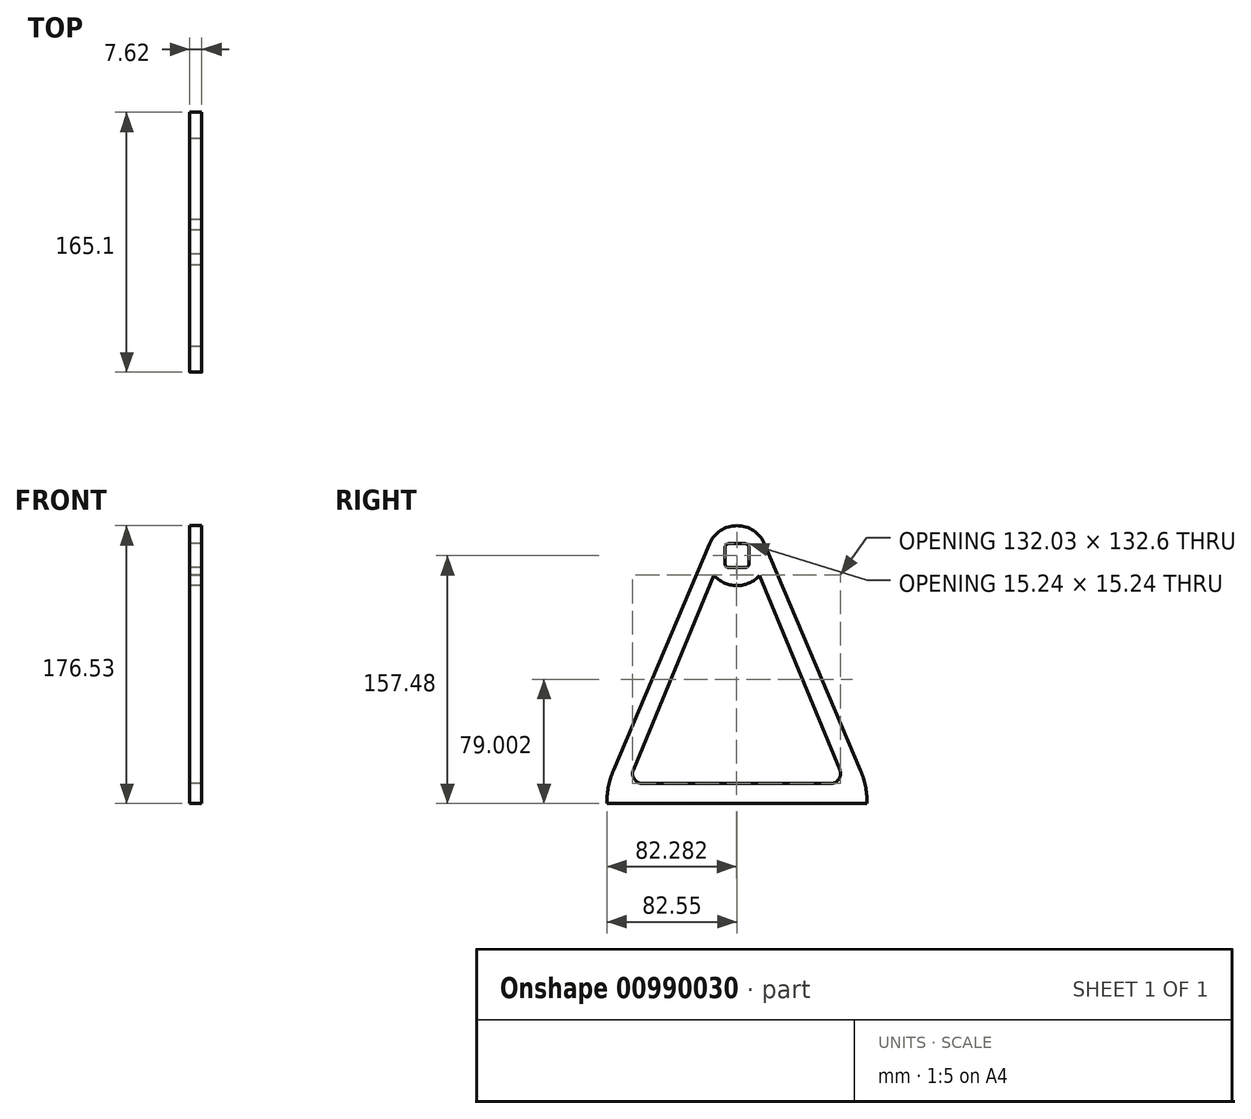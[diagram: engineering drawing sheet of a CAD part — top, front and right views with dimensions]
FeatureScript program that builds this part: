
annotation { "Feature Type Name" : "Feature", "Feature Type Description" : "" }
export const myFeature = defineFeature(function(context is Context, id is Id, definition is map)
    precondition{}
    {
        {
            var Q0;
            Q0=qCreatedBy(makeId("Right.planeOp"),FACE);
            var sketch = newSketch(context, id + "F0", { "sketchPlane" : qUnion([Q0])});
            skLineSegment(sketch, "E0.bottom", {"start": v(-3.81, 6.35) * mm, "end": v(3.81, 6.35) * mm});
            skLineSegment(sketch, "E0.top", {"start": v(-3.81, -6.35) * mm, "end": v(3.81, -6.35) * mm});
            skLineSegment(sketch, "E0.left", {"start": v(-6.35, 3.81) * mm, "end": v(-6.35, -3.81) * mm});
            skLineSegment(sketch, "E0.right", {"start": v(6.35, 3.81) * mm, "end": v(6.35, -3.81) * mm});
            skLineSegment(sketch, "E1.bottom", {"start": v(-4.76, 4.76) * mm, "end": v(4.76, 4.76) * mm});
            skLineSegment(sketch, "E1.top", {"start": v(-4.76, -4.76) * mm, "end": v(4.76, -4.76) * mm});
            skLineSegment(sketch, "E1.left", {"start": v(-4.76, 4.76) * mm, "end": v(-4.76, -4.76) * mm});
            skLineSegment(sketch, "E1.right", {"start": v(4.76, 4.76) * mm, "end": v(4.76, -4.76) * mm});
            skPoint(sketch, "E2.visualSharp", {"position": v(-6.35, 6.35) * mm});
            skArc(sketch, "E2.filletArc", {"start": v(-3.81, 6.35) * mm, "mid": v(-5.6, 5.6) * mm, "end": v(-6.35, 3.81) * mm});
            skPoint(sketch, "E3.visualSharp", {"position": v(6.35, 6.35) * mm});
            skArc(sketch, "E3.filletArc", {"start": v(6.35, 3.81) * mm, "mid": v(5.6, 5.6) * mm, "end": v(3.81, 6.35) * mm});
            skPoint(sketch, "E4.visualSharp", {"position": v(6.35, -6.35) * mm});
            skArc(sketch, "E4.filletArc", {"start": v(3.81, -6.35) * mm, "mid": v(5.6, -5.6) * mm, "end": v(6.35, -3.81) * mm});
            skPoint(sketch, "E5.visualSharp", {"position": v(-6.35, -6.35) * mm});
            skArc(sketch, "E5.filletArc", {"start": v(-6.35, -3.81) * mm, "mid": v(-5.6, -5.6) * mm, "end": v(-3.81, -6.35) * mm});
            skSolve(sketch);
        }
        {
            var Q0;
            Q0=qCreatedBy(makeId("Right.planeOp"),FACE);
            var sketch = newSketch(context, id + "F1", { "sketchPlane" : qUnion([Q0])});
            skLineSegment(sketch, "E6.bottom", {"start": v(0, -144.78) * mm, "end": v(59.43, -144.78) * mm});
            skLineSegment(sketch, "E6.top", {"start": v(0, -157.48) * mm, "end": v(82.55, -157.48) * mm});
            skLineSegment(sketch, "E6.right", {"start": v(82.55, -156.36) * mm, "end": v(82.55, -157.48) * mm});
            skLineSegment(sketch, "E7.MirrorCS", {"start": v(0, -144.78) * mm, "end": v(-59.96, -144.78) * mm});
            skLineSegment(sketch, "E8.MirrorCS", {"start": v(-82.55, -156.36) * mm, "end": v(-82.55, -157.48) * mm});
            skLineSegment(sketch, "E9.MirrorCS", {"start": v(0, -157.48) * mm, "end": v(-82.55, -157.48) * mm});
            skLineSegment(sketch, "E10", {"start": v(17.55, 7.42) * mm, "end": v(78.53, -136.55) * mm});
            skLineSegment(sketch, "E11", {"start": v(-17.54, 7.43) * mm, "end": v(-78.53, -136.55) * mm});
            skCircle(sketch, "E12", {"center": v(0, 0) * mm, "radius": 19.05 * mm});
            skLineSegment(sketch, "E13", {"start": v(14.29, -12.6) * mm, "end": v(65.3, -136) * mm});
            skLineSegment(sketch, "E14", {"start": v(-14.65, -12.18) * mm, "end": v(-65.83, -136) * mm});
            skPoint(sketch, "E15.visualSharp", {"position": v(-82.55, -146.05) * mm});
            skArc(sketch, "E15.filletArc", {"start": v(-78.53, -136.55) * mm, "mid": v(-81.53, -146.26) * mm, "end": v(-82.55, -156.36) * mm});
            skPoint(sketch, "E16.visualSharp", {"position": v(82.55, -146.05) * mm});
            skArc(sketch, "E16.filletArc", {"start": v(82.55, -156.36) * mm, "mid": v(81.53, -146.26) * mm, "end": v(78.53, -136.55) * mm});
            skPoint(sketch, "E17.newPointB", {"position": v(82.55, -144.78) * mm});
            skArc(sketch, "E17.filletArc", {"start": v(59.43, -144.78) * mm, "mid": v(64.7, -141.96) * mm, "end": v(65.3, -136) * mm});
            skPoint(sketch, "E18.newPointB", {"position": v(-82.55, -144.78) * mm});
            skArc(sketch, "E18.filletArc", {"start": v(-65.83, -136) * mm, "mid": v(-65.24, -141.96) * mm, "end": v(-59.96, -144.78) * mm});
            skLineSegment(sketch, "E19.bottom", {"start": v(-5.08, 7.62) * mm, "end": v(5.08, 7.62) * mm});
            skLineSegment(sketch, "E19.top", {"start": v(-5.08, -7.62) * mm, "end": v(5.08, -7.62) * mm});
            skLineSegment(sketch, "E19.left", {"start": v(-7.62, 5.08) * mm, "end": v(-7.62, -5.08) * mm});
            skLineSegment(sketch, "E19.right", {"start": v(7.62, 5.08) * mm, "end": v(7.62, -5.08) * mm});
            skPoint(sketch, "E20.visualSharp", {"position": v(-7.62, -7.62) * mm});
            skArc(sketch, "E20.filletArc", {"start": v(-7.62, -5.08) * mm, "mid": v(-6.88, -6.88) * mm, "end": v(-5.08, -7.62) * mm});
            skPoint(sketch, "E21.visualSharp", {"position": v(7.62, 7.62) * mm});
            skArc(sketch, "E21.filletArc", {"start": v(7.62, 5.08) * mm, "mid": v(6.88, 6.88) * mm, "end": v(5.08, 7.62) * mm});
            skPoint(sketch, "E22.visualSharp", {"position": v(-7.62, 7.62) * mm});
            skArc(sketch, "E22.filletArc", {"start": v(-5.08, 7.62) * mm, "mid": v(-6.88, 6.88) * mm, "end": v(-7.62, 5.08) * mm});
            skPoint(sketch, "E23.visualSharp", {"position": v(7.62, -7.62) * mm});
            skArc(sketch, "E23.filletArc", {"start": v(5.08, -7.62) * mm, "mid": v(6.88, -6.88) * mm, "end": v(7.62, -5.08) * mm});
            skSolve(sketch);
        }
        {
            var Q0;
            Q0=makeQuery(id+"F1.imprint","IMPRINT",FACE,{"disambiguationData":[TD([[makeQuery(id+"F1.imprint","IMPRINT",EDGE,{"derivedFrom":sQuery(id+"F1.wireOp",EDGE,"19484ca9-c6df-4c4f-9a82-6452225bbd83")}),-1.0]])]});
            var Q1;
            Q1=makeQuery(id+"F1.imprint","IMPRINT",FACE,{"disambiguationData":[TD([[makeQuery(id+"F1.imprint","IMPRINT",EDGE,{"derivedFrom":sQuery(id+"F1.wireOp",EDGE,"E6.bottom")}),-1.0]])]});
            extrude(context, id + "F2", {"entities" : qUnion([Q0, Q1]), "depth" : 7.62 * mm, "offsetDistance" : 25.4 * mm});
        }
        {
            var Q0;
            Q0=makeQuery(id+"F1.imprint","IMPRINT",FACE,{"disambiguationData":[TD([[makeQuery(id+"F1.imprint","IMPRINT",EDGE,{"derivedFrom":sQuery(id+"F1.wireOp",EDGE,"E19.bottom")}),1.0]])]});
            extrude(context, id + "F3", {"entities" : qUnion([Q0]), "operationType" : NewBodyOperationType.ADD, "depth" : 7.62 * mm, "offsetDistance" : 25.4 * mm});
        }
    });
